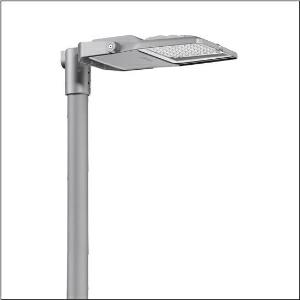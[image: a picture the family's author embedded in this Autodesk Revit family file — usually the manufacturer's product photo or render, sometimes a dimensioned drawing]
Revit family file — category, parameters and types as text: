
# Revit family: floodlight_fl_21_iq_mini___pl61_5xa7772c4c3a_2e37
name_source: partatom
category: Lighting Fixtures
units: mm (PartAtom-declared; Revit-internal decimal feet)

## family parameters
Cut with Voids When Loaded = No
Host = Face
Light Source = No
Part Type = Normal
Room Calculation Point = No
Round Connector Dimension = Use Diameter
Shared = No

## types (1)
- --- (1 x LED, 12490 lm, 87.2 W, 4000K)
    Apparent Load = 87 VA
    CIE Flux Codes = 33 65 98 100 100
    Color Rendering = 70
    Color Temperature = 4000K
    Default Elevation = 1800 mm
    Description = Floodlight FL 21 iQ mini, floodlight, primary light control with lens, of PMMA, primary optical cover: protective disc, of toughened safety glass, transparent, light distribution: PL61, light emission: direct distribution, installation type: surface-mounted, LED, High Power LED, rated luminous flux: 12.490lm, luminous efficacy: 143lm/W, light colour: 740, colour temperature: 4000K, control: Auto-Match, Temp-Guard, Night-Set, Smart-Wire, Desk-Remote (wireless, voltage-free reading and setting of iQ features in the workshop via application-optimized NFC function/RFID function), optimised constant luminous flux control (CLO 2.0), Light-Fading, Lumen-Switch, with terminal, 6-pole, mains connection: 220..240V, AC, 50/60Hz, start of lifetime: 87W, end of service life: 92W, reduction: 40W, luminaire housing, of diecast aluminium, powder-coated, Siteco® metallic grey (DB 702S), corrosivity category C5 mid according to DIN EN ISO 12944, sealing non-destructively replaceable, please order mast flange separately, mast bracket, of steel, galvanised, powder-coated, protection rating (complete): IP66, insulation class (complete): insulation class II (safety insulation), certification: CE, ENEC, VDE, protection symbol: D, impact resistance: IK08, permissible operating ambient temperature: -40..+40°C, permissible operating ambient temperature for outdoor applications: -40..+50°C, standard: DIN EN 12944, LABS conformity tested according to VDMA 24364:2018-05, packaging unit: 1 piece

Light Distribution: PL61
    Height = 70 mm
    Lamp = 1 x LED
    Lamp Light Flux = 12490 lm
    Lamp Power = 87.2 W
    Lamp count = 1
    Length = 485 mm
    Luminous efficacy = 143 lm/W
    Manufacturer = Siteco
    ModVariant = No
    Model = 5XA7772C4C3A
    Number of Poles = 1
    OnlyDefault = Yes
    Power Factor = 1
    Product Name = Floodlight FL 21 iQ mini | PL61
    Product group = floodlight | pylon annexe
    ProductGroupID = 6200
    Protection Class = Protection class II
    Protection Degree = IP 66
    RLX_Detail_Level = 1
    RLX_Emergency_Light_Flux = 0 lm
    RLX_Emergency_Type = 0
    RLX_Emergency_Type_DB = No
    RlxData = <blob elided: 101445 chars, md5=0fdf4f0e>
    Socket = socket
    Standby Power = 0 W
    System Light Flux = 12490 lm
    System Power = 87 W
    Type Comments = factory setting: luminous flux: 100 % | dim-lin: 254 | 456 mA
    Type Image = l_1007125.jpg
    URL = http://relux.com
    VarID = @adj_105975
    Voltage = 0 V
    Weight = 0.00 kg
    Width = 337 mm

## geometry (parser evidence)
native form markers: Blend x4, Sweep x10
no freeform markers — native parametric forms only
